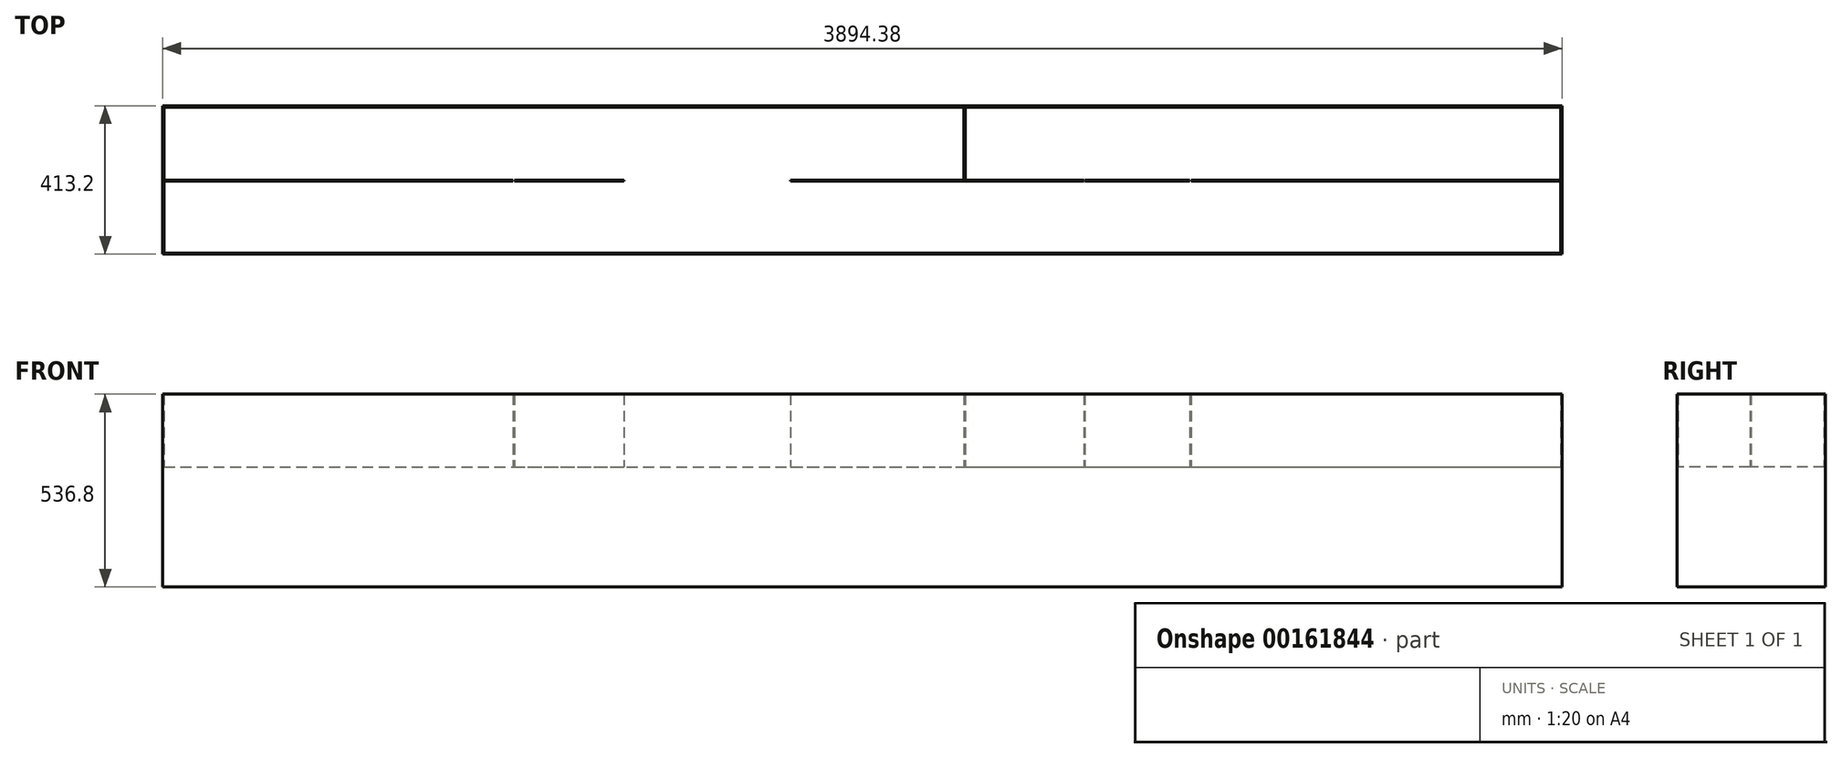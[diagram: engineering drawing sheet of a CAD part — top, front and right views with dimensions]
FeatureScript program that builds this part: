
annotation { "Feature Type Name" : "Feature", "Feature Type Description" : "" }
export const myFeature = defineFeature(function(context is Context, id is Id, definition is map)
    precondition{}
    {
        {
            var Q0;
            Q0=qCreatedBy(makeId("Top.planeOp"),FACE);
            var sketch = newSketch(context, id + "F0", { "sketchPlane" : qUnion([Q0])});
            skLineSegment(sketch, "E0.bottom", {"start": v(-1943.79, 203.2) * mm, "end": v(1943.79, 203.2) * mm});
            skLineSegment(sketch, "E0.top", {"start": v(-1943.79, -203.2) * mm, "end": v(1943.79, -203.2) * mm});
            skLineSegment(sketch, "E0.left", {"start": v(-1943.79, 203.2) * mm, "end": v(-1943.79, -203.2) * mm});
            skLineSegment(sketch, "E0.right", {"start": v(1943.79, 203.2) * mm, "end": v(1943.79, -203.2) * mm});
            skPoint(sketch, "E0.middle", {"position": v(0, 0) * mm});
            skLineSegment(sketch, "E1.bottom", {"start": v(-968.83, 203.2) * mm, "end": v(-972.24, 203.2) * mm});
            skLineSegment(sketch, "E1.top", {"start": v(-968.83, -203.2) * mm, "end": v(-972.24, -203.2) * mm});
            skLineSegment(sketch, "E1.left", {"start": v(-968.83, 203.2) * mm, "end": v(-968.83, -203.2) * mm});
            skLineSegment(sketch, "E1.right", {"start": v(-972.24, 203.2) * mm, "end": v(-972.24, -203.2) * mm});
            skLineSegment(sketch, "E2.bottom", {"start": v(-1943.79, 0) * mm, "end": v(-972.24, 0) * mm});
            skLineSegment(sketch, "E2.top", {"start": v(-1943.79, -3.4) * mm, "end": v(-972.24, -3.4) * mm});
            skLineSegment(sketch, "E2.left", {"start": v(-1943.79, 0) * mm, "end": v(-1943.79, -3.4) * mm});
            skLineSegment(sketch, "E2.right", {"start": v(-972.24, 0) * mm, "end": v(-972.24, -3.4) * mm});
            skLineSegment(sketch, "E3.bottom", {"start": v(-664.03, 203.2) * mm, "end": v(-660.63, 203.2) * mm});
            skLineSegment(sketch, "E3.top", {"start": v(-664.03, -203.2) * mm, "end": v(-660.63, -203.2) * mm});
            skLineSegment(sketch, "E3.left", {"start": v(-664.03, 203.2) * mm, "end": v(-664.03, -203.2) * mm});
            skLineSegment(sketch, "E3.right", {"start": v(-660.63, 203.2) * mm, "end": v(-660.63, -203.2) * mm});
            skLineSegment(sketch, "E4.bottom", {"start": v(-968.83, 0) * mm, "end": v(-664.03, 0) * mm});
            skLineSegment(sketch, "E4.top", {"start": v(-968.83, -3.4) * mm, "end": v(-664.03, -3.4) * mm});
            skLineSegment(sketch, "E4.left", {"start": v(-968.83, 0) * mm, "end": v(-968.83, -3.4) * mm});
            skLineSegment(sketch, "E4.right", {"start": v(-664.03, 0) * mm, "end": v(-664.03, -3.4) * mm});
            skLineSegment(sketch, "E5.bottom", {"start": v(-203.43, 203.2) * mm, "end": v(-200.02, 203.2) * mm});
            skLineSegment(sketch, "E5.top", {"start": v(-203.43, -203.2) * mm, "end": v(-200.02, -203.2) * mm});
            skLineSegment(sketch, "E5.left", {"start": v(-203.43, 203.2) * mm, "end": v(-203.43, -203.2) * mm});
            skLineSegment(sketch, "E5.right", {"start": v(-200.02, 203.2) * mm, "end": v(-200.03, -203.2) * mm});
            skLineSegment(sketch, "E6.bottom", {"start": v(-200.03, 0) * mm, "end": v(282.58, 0) * mm});
            skLineSegment(sketch, "E6.top", {"start": v(-200.03, -3.4) * mm, "end": v(282.58, -3.4) * mm});
            skLineSegment(sketch, "E6.left", {"start": v(-200.03, 0) * mm, "end": v(-200.03, -3.4) * mm});
            skLineSegment(sketch, "E6.right", {"start": v(282.58, 0) * mm, "end": v(282.58, -3.4) * mm});
            skLineSegment(sketch, "E7.bottom", {"start": v(282.58, 203.2) * mm, "end": v(285.98, 203.2) * mm});
            skLineSegment(sketch, "E7.left", {"start": v(282.58, 203.2) * mm, "end": v(282.58, 0) * mm});
            skLineSegment(sketch, "E7.right", {"start": v(285.98, 203.2) * mm, "end": v(285.98, -3.4) * mm});
            skLineSegment(sketch, "E8", {"start": v(285.98, -3.4) * mm, "end": v(282.58, -3.4) * mm});
            skLineSegment(sketch, "E9.bottom", {"start": v(-126.77, -3.4) * mm, "end": v(-130.17, -3.4) * mm});
            skLineSegment(sketch, "E9.top", {"start": v(-126.77, -203.2) * mm, "end": v(-130.18, -203.2) * mm});
            skLineSegment(sketch, "E9.left", {"start": v(-126.77, -3.4) * mm, "end": v(-126.77, -203.2) * mm});
            skLineSegment(sketch, "E9.right", {"start": v(-130.17, -3.4) * mm, "end": v(-130.18, -203.2) * mm});
            skLineSegment(sketch, "E10.bottom", {"start": v(168.73, -3.4) * mm, "end": v(165.33, -3.4) * mm});
            skLineSegment(sketch, "E10.top", {"start": v(168.73, -203.2) * mm, "end": v(165.33, -203.2) * mm});
            skLineSegment(sketch, "E10.left", {"start": v(168.73, -3.4) * mm, "end": v(168.73, -203.2) * mm});
            skLineSegment(sketch, "E10.right", {"start": v(165.33, -3.4) * mm, "end": v(165.33, -203.2) * mm});
            skLineSegment(sketch, "E11.bottom", {"start": v(616.18, 203.2) * mm, "end": v(619.58, 203.2) * mm});
            skLineSegment(sketch, "E11.top", {"start": v(616.18, -203.2) * mm, "end": v(619.58, -203.2) * mm});
            skLineSegment(sketch, "E11.left", {"start": v(616.18, 203.2) * mm, "end": v(616.18, -203.2) * mm});
            skLineSegment(sketch, "E11.right", {"start": v(619.58, 203.2) * mm, "end": v(619.58, -203.2) * mm});
            skLineSegment(sketch, "E12.bottom", {"start": v(285.98, 0) * mm, "end": v(616.18, 0) * mm});
            skLineSegment(sketch, "E12.top", {"start": v(285.98, -3.4) * mm, "end": v(616.18, -3.4) * mm});
            skLineSegment(sketch, "E12.left", {"start": v(285.98, 0) * mm, "end": v(285.98, -3.4) * mm});
            skLineSegment(sketch, "E12.right", {"start": v(616.18, 0) * mm, "end": v(616.18, -3.4) * mm});
            skLineSegment(sketch, "E13.bottom", {"start": v(911.68, 203.2) * mm, "end": v(915.09, 203.2) * mm});
            skLineSegment(sketch, "E13.top", {"start": v(911.68, -203.2) * mm, "end": v(915.09, -203.2) * mm});
            skLineSegment(sketch, "E13.left", {"start": v(911.68, 203.2) * mm, "end": v(911.68, -203.2) * mm});
            skLineSegment(sketch, "E13.right", {"start": v(915.09, 203.2) * mm, "end": v(915.09, -203.2) * mm});
            skPoint(sketch, "E14.oppositeSnap0", {"position": v(911.68, 0) * mm});
            skLineSegment(sketch, "E14.bottom", {"start": v(619.58, 0) * mm, "end": v(911.68, 0) * mm});
            skLineSegment(sketch, "E14.top", {"start": v(619.58, -3.4) * mm, "end": v(911.68, -3.4) * mm});
            skLineSegment(sketch, "E14.left", {"start": v(619.58, 0) * mm, "end": v(619.58, -3.4) * mm});
            skLineSegment(sketch, "E14.right", {"start": v(911.68, 0) * mm, "end": v(911.68, -3.4) * mm});
            skLineSegment(sketch, "E15.bottom", {"start": v(915.09, -3.4) * mm, "end": v(1943.79, -3.4) * mm});
            skLineSegment(sketch, "E15.top", {"start": v(915.09, 0) * mm, "end": v(1943.79, 0) * mm});
            skLineSegment(sketch, "E15.left", {"start": v(915.09, -3.4) * mm, "end": v(915.09, 0) * mm});
            skLineSegment(sketch, "E15.right", {"start": v(1943.79, -3.4) * mm, "end": v(1943.79, 0) * mm});
            skLineSegment(sketch, "E16.bottom", {"start": v(-1947.19, 206.6) * mm, "end": v(1947.19, 206.6) * mm});
            skLineSegment(sketch, "E16.top", {"start": v(-1947.19, -206.6) * mm, "end": v(1947.19, -206.6) * mm});
            skLineSegment(sketch, "E16.left", {"start": v(-1947.19, 206.6) * mm, "end": v(-1947.19, -206.6) * mm});
            skLineSegment(sketch, "E16.right", {"start": v(1947.19, 206.6) * mm, "end": v(1947.19, -206.6) * mm});
            skSolve(sketch);
        }
        {
            var Q0;
            Q0 = qSketchRegion(id + "F0", true);
            var Q1;
            Q1=makeQuery(id+"F0.imprint","IMPRINT",FACE,{"disambiguationData":[TD([[makeQuery(id+"F0.imprint","IMPRINT",EDGE,{"derivedFrom":sQuery(id+"F0.wireOp",EDGE,"E2.bottom")}),-1.0]])]});
            var Q2;
            {var subQ5=sQuery(id+"F0.wireOp",EDGE,"E1.bottom");Q2=makeQuery(id+"F0.imprint","IMPRINT",FACE,{"disambiguationData":[TD([[makeQuery(id+"F0.imprint","IMPRINT",EDGE,{"derivedFrom":subQ5}),1.0]])]});}
            var Q3;
            Q3=makeQuery(id+"F0.imprint","IMPRINT",FACE,{"disambiguationData":[TD([[makeQuery(id+"F0.imprint","IMPRINT",EDGE,{"derivedFrom":sQuery(id+"F0.wireOp",EDGE,"E4.bottom")}),-1.0]])]});
            var Q4;
            {var subQ3=sQuery(id+"F0.wireOp",EDGE,"E3.bottom");Q4=makeQuery(id+"F0.imprint","IMPRINT",FACE,{"disambiguationData":[TD([[makeQuery(id+"F0.imprint","IMPRINT",EDGE,{"derivedFrom":subQ3}),-1.0]])]});}
            var Q5;
            {var subQ1=sQuery(id+"F0.wireOp",EDGE,"E5.bottom");Q5=makeQuery(id+"F0.imprint","IMPRINT",FACE,{"disambiguationData":[TD([[makeQuery(id+"F0.imprint","IMPRINT",EDGE,{"derivedFrom":subQ1}),-1.0]])]});}
            var Q6;
            Q6=makeQuery(id+"F0.imprint","IMPRINT",FACE,{"disambiguationData":[TD([[makeQuery(id+"F0.imprint","IMPRINT",EDGE,{"derivedFrom":sQuery(id+"F0.wireOp",EDGE,"E6.bottom")}),-1.0]])]});
            var Q7;
            Q7=makeQuery(id+"F0.imprint","IMPRINT",FACE,{"disambiguationData":[TD([[makeQuery(id+"F0.imprint","IMPRINT",EDGE,{"derivedFrom":sQuery(id+"F0.wireOp",EDGE,"E9.bottom")}),1.0]])]});
            var Q8;
            Q8=makeQuery(id+"F0.imprint","IMPRINT",FACE,{"disambiguationData":[TD([[makeQuery(id+"F0.imprint","IMPRINT",EDGE,{"derivedFrom":sQuery(id+"F0.wireOp",EDGE,"E10.bottom")}),1.0]])]});
            var Q9;
            Q9=makeQuery(id+"F0.imprint","IMPRINT",FACE,{"disambiguationData":[TD([[makeQuery(id+"F0.imprint","IMPRINT",EDGE,{"derivedFrom":sQuery(id+"F0.wireOp",EDGE,"E6.right")}),1.0]])]});
            var Q10;
            Q10=makeQuery(id+"F0.imprint","IMPRINT",FACE,{"disambiguationData":[TD([[makeQuery(id+"F0.imprint","IMPRINT",EDGE,{"derivedFrom":sQuery(id+"F0.wireOp",EDGE,"E12.bottom")}),-1.0]])]});
            var Q11;
            {var subQ5=sQuery(id+"F0.wireOp",EDGE,"E11.bottom");Q11=makeQuery(id+"F0.imprint","IMPRINT",FACE,{"disambiguationData":[TD([[makeQuery(id+"F0.imprint","IMPRINT",EDGE,{"derivedFrom":subQ5}),-1.0]])]});}
            var Q12;
            Q12=makeQuery(id+"F0.imprint","IMPRINT",FACE,{"disambiguationData":[TD([[makeQuery(id+"F0.imprint","IMPRINT",EDGE,{"derivedFrom":sQuery(id+"F0.wireOp",EDGE,"E14.bottom")}),-1.0]])]});
            var Q13;
            {var subQ4=sQuery(id+"F0.wireOp",EDGE,"E13.bottom");Q13=makeQuery(id+"F0.imprint","IMPRINT",FACE,{"disambiguationData":[TD([[makeQuery(id+"F0.imprint","IMPRINT",EDGE,{"derivedFrom":subQ4}),-1.0]])]});}
            var Q14;
            Q14=makeQuery(id+"F0.imprint","IMPRINT",FACE,{"disambiguationData":[TD([[makeQuery(id+"F0.imprint","IMPRINT",EDGE,{"derivedFrom":sQuery(id+"F0.wireOp",EDGE,"E15.bottom")}),1.0]])]});
            extrude(context, id + "F1", {"entities" : qUnion([Q0, Q1, Q2, Q3, Q4, Q5, Q6, Q7, Q8, Q9, Q10, Q11, Q12, Q13, Q14]), "depth" : 533.4 * mm});
        }
        {
            var Q0;
            Q0=makeQuery(id+"F1.opExtrude","CAP_FACE",FACE,{"disambiguationData":[OSD([sQuery(id+"F0.wireOp",EDGE,"E0.bottom"),sQuery(id+"F0.wireOp",EDGE,"E0.top"),sQuery(id+"F0.wireOp",EDGE,"E0.left"),sQuery(id+"F0.wireOp",EDGE,"E0.right"),sQuery(id+"F0.wireOp",EDGE,"E1.left"),sQuery(id+"F0.wireOp",EDGE,"E1.right"),sQuery(id+"F0.wireOp",EDGE,"E2.bottom"),sQuery(id+"F0.wireOp",EDGE,"E2.top"),sQuery(id+"F0.wireOp",EDGE,"E3.left"),sQuery(id+"F0.wireOp",EDGE,"E3.right"),sQuery(id+"F0.wireOp",EDGE,"E4.bottom"),sQuery(id+"F0.wireOp",EDGE,"E4.top"),sQuery(id+"F0.wireOp",EDGE,"E5.left"),sQuery(id+"F0.wireOp",EDGE,"E5.right"),sQuery(id+"F0.wireOp",EDGE,"E6.bottom"),sQuery(id+"F0.wireOp",EDGE,"E6.top"),sQuery(id+"F0.wireOp",EDGE,"E7.left"),sQuery(id+"F0.wireOp",EDGE,"E7.right"),sQuery(id+"F0.wireOp",EDGE,"E8"),sQuery(id+"F0.wireOp",EDGE,"E9.left"),sQuery(id+"F0.wireOp",EDGE,"E9.right"),sQuery(id+"F0.wireOp",EDGE,"E10.left"),sQuery(id+"F0.wireOp",EDGE,"E10.right"),sQuery(id+"F0.wireOp",EDGE,"E11.left"),sQuery(id+"F0.wireOp",EDGE,"E11.right"),sQuery(id+"F0.wireOp",EDGE,"E12.bottom"),sQuery(id+"F0.wireOp",EDGE,"E12.top"),sQuery(id+"F0.wireOp",EDGE,"E13.left"),sQuery(id+"F0.wireOp",EDGE,"E13.right"),sQuery(id+"F0.wireOp",EDGE,"E14.bottom"),sQuery(id+"F0.wireOp",EDGE,"E14.top"),sQuery(id+"F0.wireOp",EDGE,"E15.bottom"),sQuery(id+"F0.wireOp",EDGE,"E15.top"),sQuery(id+"F0.wireOp",EDGE,"E16.bottom"),sQuery(id+"F0.wireOp",EDGE,"E16.top"),sQuery(id+"F0.wireOp",EDGE,"E16.left"),sQuery(id+"F0.wireOp",EDGE,"E16.right")])],"isStart":true});
            var sketch = newSketch(context, id + "F2", { "sketchPlane" : qUnion([Q0])});
            skLineSegment(sketch, "E17.bottom", {"start": v(-1947.19, 206.6) * mm, "end": v(1947.19, 206.6) * mm});
            skLineSegment(sketch, "E17.top", {"start": v(-1947.19, -206.6) * mm, "end": v(1947.19, -206.6) * mm});
            skLineSegment(sketch, "E17.left", {"start": v(-1947.19, 206.6) * mm, "end": v(-1947.19, -206.6) * mm});
            skLineSegment(sketch, "E17.right", {"start": v(1947.19, 206.6) * mm, "end": v(1947.19, -206.6) * mm});
            skSolve(sketch);
        }
        {
            var Q0;
            Q0 = qSketchRegion(id + "F2", true);
            extrude(context, id + "F3", {"entities" : qUnion([Q0]), "operationType" : NewBodyOperationType.ADD, "depth" : 3.4 * mm});
        }
        {
            var Q0;
            {var subQ5=sQuery(id+"F0.wireOp",EDGE,"E14.bottom");Q0=makeQuery(id+"F3.boolean.opBoolean","SPLIT",FACE,{"disambiguationData":[TD([makeQuery(id+"F1.opExtrude","SWEPT_FACE",FACE,{"disambiguationData":[OSD([subQ5])]})])],"derivedFrom":makeQuery(id+"F3.opExtrude","CAP_FACE",FACE,{"disambiguationData":[OSD([sQuery(id+"F2.wireOp",EDGE,"E17.bottom"),sQuery(id+"F2.wireOp",EDGE,"E17.top"),sQuery(id+"F2.wireOp",EDGE,"E17.left"),sQuery(id+"F2.wireOp",EDGE,"E17.right")])],"isStart":true})});}
            var Q1;
            {var subQ5=sQuery(id+"F0.wireOp",EDGE,"E14.top");Q1=makeQuery(id+"F3.boolean.opBoolean","SPLIT",FACE,{"disambiguationData":[TD([makeQuery(id+"F1.opExtrude","SWEPT_FACE",FACE,{"disambiguationData":[OSD([subQ5])]})])],"derivedFrom":makeQuery(id+"F3.opExtrude","CAP_FACE",FACE,{"disambiguationData":[OSD([sQuery(id+"F2.wireOp",EDGE,"E17.bottom"),sQuery(id+"F2.wireOp",EDGE,"E17.top"),sQuery(id+"F2.wireOp",EDGE,"E17.left"),sQuery(id+"F2.wireOp",EDGE,"E17.right")])],"isStart":true})});}
            var Q2;
            {var subQ0=sQuery(id+"F0.wireOp",EDGE,"E10.left");Q2=makeQuery(id+"F3.boolean.opBoolean","SPLIT",FACE,{"disambiguationData":[TD([makeQuery(id+"F1.opExtrude","SWEPT_FACE",FACE,{"disambiguationData":[OSD([subQ0])]})])],"derivedFrom":makeQuery(id+"F3.opExtrude","CAP_FACE",FACE,{"disambiguationData":[OSD([sQuery(id+"F2.wireOp",EDGE,"E17.bottom"),sQuery(id+"F2.wireOp",EDGE,"E17.top"),sQuery(id+"F2.wireOp",EDGE,"E17.left"),sQuery(id+"F2.wireOp",EDGE,"E17.right")])],"isStart":true})});}
            var Q3;
            {var subQ0=sQuery(id+"F0.wireOp",EDGE,"E7.right");Q3=makeQuery(id+"F3.boolean.opBoolean","SPLIT",FACE,{"disambiguationData":[TD([makeQuery(id+"F1.opExtrude","SWEPT_FACE",FACE,{"disambiguationData":[OSD([subQ0])]})])],"derivedFrom":makeQuery(id+"F3.opExtrude","CAP_FACE",FACE,{"disambiguationData":[OSD([sQuery(id+"F2.wireOp",EDGE,"E17.bottom"),sQuery(id+"F2.wireOp",EDGE,"E17.top"),sQuery(id+"F2.wireOp",EDGE,"E17.left"),sQuery(id+"F2.wireOp",EDGE,"E17.right")])],"isStart":true})});}
            var Q4;
            {var subQ4=sQuery(id+"F0.wireOp",EDGE,"E6.bottom");Q4=makeQuery(id+"F3.boolean.opBoolean","SPLIT",FACE,{"disambiguationData":[TD([makeQuery(id+"F1.opExtrude","SWEPT_FACE",FACE,{"disambiguationData":[OSD([subQ4])]})])],"derivedFrom":makeQuery(id+"F3.opExtrude","CAP_FACE",FACE,{"disambiguationData":[OSD([sQuery(id+"F2.wireOp",EDGE,"E17.bottom"),sQuery(id+"F2.wireOp",EDGE,"E17.top"),sQuery(id+"F2.wireOp",EDGE,"E17.left"),sQuery(id+"F2.wireOp",EDGE,"E17.right")])],"isStart":true})});}
            var Q5;
            {var subQ0=sQuery(id+"F0.wireOp",EDGE,"E9.left");Q5=makeQuery(id+"F3.boolean.opBoolean","SPLIT",FACE,{"disambiguationData":[TD([makeQuery(id+"F1.opExtrude","SWEPT_FACE",FACE,{"disambiguationData":[OSD([subQ0])]})])],"derivedFrom":makeQuery(id+"F3.opExtrude","CAP_FACE",FACE,{"disambiguationData":[OSD([sQuery(id+"F2.wireOp",EDGE,"E17.bottom"),sQuery(id+"F2.wireOp",EDGE,"E17.top"),sQuery(id+"F2.wireOp",EDGE,"E17.left"),sQuery(id+"F2.wireOp",EDGE,"E17.right")])],"isStart":true})});}
            var Q6;
            {var subQ3=sQuery(id+"F0.wireOp",EDGE,"E9.right");Q6=makeQuery(id+"F3.boolean.opBoolean","SPLIT",FACE,{"disambiguationData":[TD([makeQuery(id+"F1.opExtrude","SWEPT_FACE",FACE,{"disambiguationData":[OSD([subQ3])]})])],"derivedFrom":makeQuery(id+"F3.opExtrude","CAP_FACE",FACE,{"disambiguationData":[OSD([sQuery(id+"F2.wireOp",EDGE,"E17.bottom"),sQuery(id+"F2.wireOp",EDGE,"E17.top"),sQuery(id+"F2.wireOp",EDGE,"E17.left"),sQuery(id+"F2.wireOp",EDGE,"E17.right")])],"isStart":true})});}
            var Q7;
            {var subQ0=sQuery(id+"F0.wireOp",EDGE,"E3.right");Q7=makeQuery(id+"F3.boolean.opBoolean","SPLIT",FACE,{"disambiguationData":[TD([makeQuery(id+"F1.opExtrude","SWEPT_FACE",FACE,{"disambiguationData":[OSD([subQ0])]})])],"derivedFrom":makeQuery(id+"F3.opExtrude","CAP_FACE",FACE,{"disambiguationData":[OSD([sQuery(id+"F2.wireOp",EDGE,"E17.bottom"),sQuery(id+"F2.wireOp",EDGE,"E17.top"),sQuery(id+"F2.wireOp",EDGE,"E17.left"),sQuery(id+"F2.wireOp",EDGE,"E17.right")])],"isStart":true})});}
            var Q8;
            {var subQ5=sQuery(id+"F0.wireOp",EDGE,"E4.bottom");Q8=makeQuery(id+"F3.boolean.opBoolean","SPLIT",FACE,{"disambiguationData":[TD([makeQuery(id+"F1.opExtrude","SWEPT_FACE",FACE,{"disambiguationData":[OSD([subQ5])]})])],"derivedFrom":makeQuery(id+"F3.opExtrude","CAP_FACE",FACE,{"disambiguationData":[OSD([sQuery(id+"F2.wireOp",EDGE,"E17.bottom"),sQuery(id+"F2.wireOp",EDGE,"E17.top"),sQuery(id+"F2.wireOp",EDGE,"E17.left"),sQuery(id+"F2.wireOp",EDGE,"E17.right")])],"isStart":true})});}
            var Q9;
            {var subQ5=sQuery(id+"F0.wireOp",EDGE,"E4.top");Q9=makeQuery(id+"F3.boolean.opBoolean","SPLIT",FACE,{"disambiguationData":[TD([makeQuery(id+"F1.opExtrude","SWEPT_FACE",FACE,{"disambiguationData":[OSD([subQ5])]})])],"derivedFrom":makeQuery(id+"F3.opExtrude","CAP_FACE",FACE,{"disambiguationData":[OSD([sQuery(id+"F2.wireOp",EDGE,"E17.bottom"),sQuery(id+"F2.wireOp",EDGE,"E17.top"),sQuery(id+"F2.wireOp",EDGE,"E17.left"),sQuery(id+"F2.wireOp",EDGE,"E17.right")])],"isStart":true})});}
            extrude(context, id + "F4", {"entities" : qUnion([Q0, Q1, Q2, Q3, Q4, Q5, Q6, Q7, Q8, Q9]), "operationType" : NewBodyOperationType.ADD, "depth" : 330.2 * mm});
        }
    });
